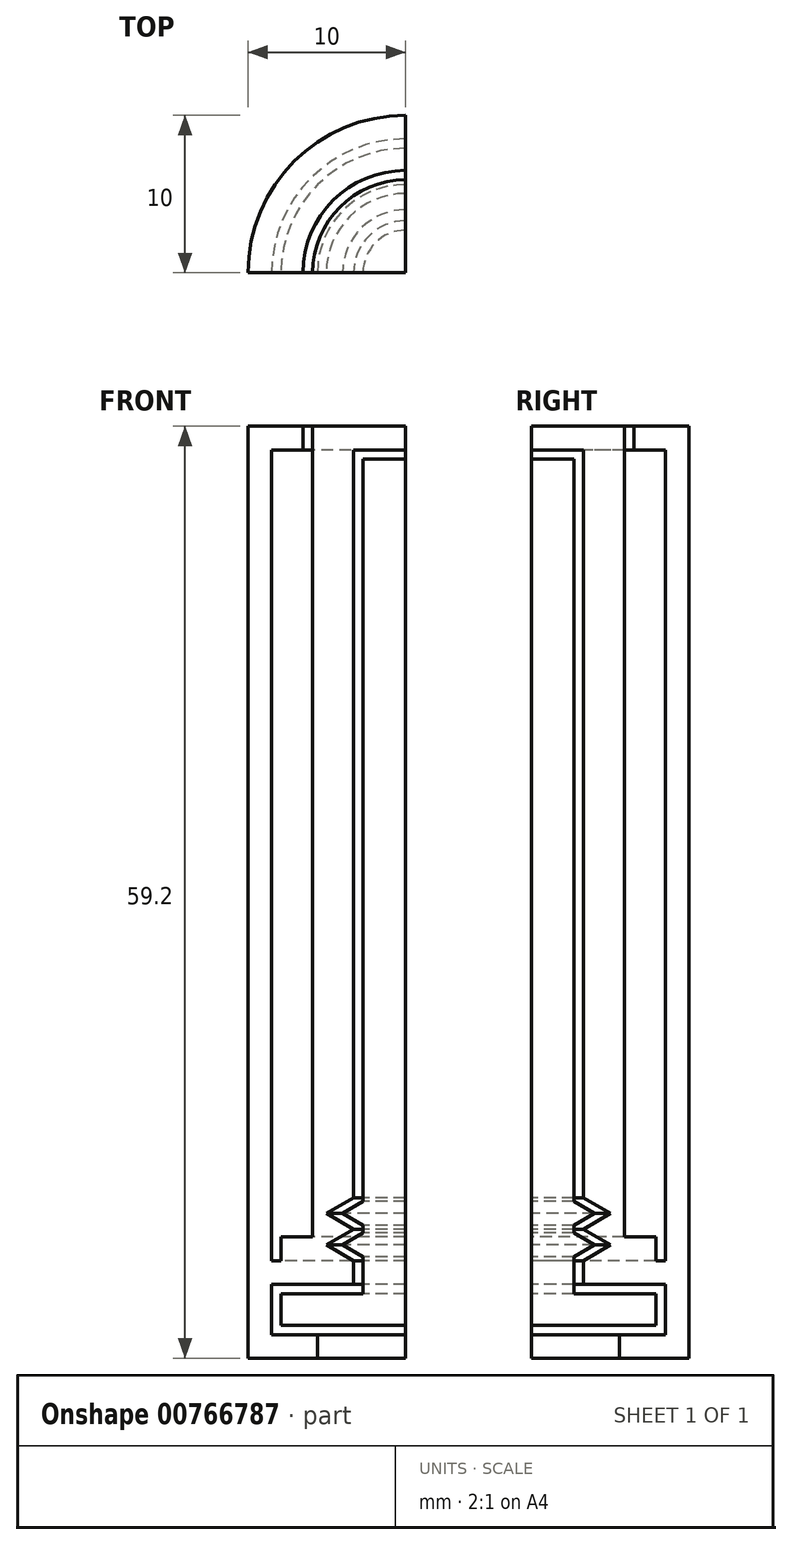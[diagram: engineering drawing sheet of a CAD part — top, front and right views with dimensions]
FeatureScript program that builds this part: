
annotation { "Feature Type Name" : "Feature", "Feature Type Description" : "" }
export const myFeature = defineFeature(function(context is Context, id is Id, definition is map)
    precondition{}
    {
        {
            var Q0;
            Q0=qCreatedBy(makeId("Front.planeOp"),FACE);
            var sketch = newSketch(context, id + "F0", { "sketchPlane" : qUnion([Q0])});
            skLineSegment(sketch, "E0", {"start": v(-3.3, -1.5) * mm, "end": v(-8.5, -1.5) * mm});
            skLineSegment(sketch, "E1", {"start": v(-8.5, -1.5) * mm, "end": v(-8.5, -4.7) * mm});
            skLineSegment(sketch, "E2", {"start": v(-8.5, -4.7) * mm, "end": v(-5.6, -4.7) * mm});
            skLineSegment(sketch, "E3", {"start": v(-5.6, -4.7) * mm, "end": v(-5.6, -6.2) * mm});
            skLineSegment(sketch, "E4", {"start": v(-5.6, -6.2) * mm, "end": v(-10, -6.2) * mm});
            skLineSegment(sketch, "E5", {"start": v(-10, -6.2) * mm, "end": v(-10, 53) * mm});
            skLineSegment(sketch, "E6", {"start": v(-10, 53) * mm, "end": v(-6.5, 53) * mm});
            skLineSegment(sketch, "E7", {"start": v(-6.5, 53) * mm, "end": v(-6.5, 51.5) * mm});
            skLineSegment(sketch, "E8", {"start": v(-6.5, 51.5) * mm, "end": v(-8.5, 51.5) * mm});
            skLineSegment(sketch, "E9", {"start": v(-8.5, 51.5) * mm, "end": v(-8.5, 0) * mm});
            skLineSegment(sketch, "E10", {"start": v(-8.5, 0) * mm, "end": v(-3.3, 0) * mm});
            skLineSegment(sketch, "E11", {"start": v(-3.3, 0) * mm, "end": v(-3.3, -1.5) * mm});
            skLineSegment(sketch, "E12", {"start": v(0, 50) * mm, "end": v(0, -50) * mm});
            skPoint(sketch, "E13", {"position": v(0, 0) * mm});
            skLineSegment(sketch, "E14", {"start": v(-7.9, 0) * mm, "end": v(-3.3, 0) * mm});
            skLineSegment(sketch, "E15", {"start": v(-3.3, 0) * mm, "end": v(-3.3, 51.5) * mm});
            skLineSegment(sketch, "E16", {"start": v(-3.3, 51.5) * mm, "end": v(0, 51.5) * mm});
            skLineSegment(sketch, "E17", {"start": v(0, 51.5) * mm, "end": v(0, 53) * mm});
            skLineSegment(sketch, "E18", {"start": v(0, 53) * mm, "end": v(-5.9, 53) * mm});
            skLineSegment(sketch, "E19", {"start": v(-5.9, 53) * mm, "end": v(-5.9, 1.5) * mm});
            skLineSegment(sketch, "E20", {"start": v(-5.9, 1.5) * mm, "end": v(-7.9, 1.5) * mm});
            skLineSegment(sketch, "E21", {"start": v(-7.9, 1.5) * mm, "end": v(-7.9, 0) * mm});
            skLineSegment(sketch, "E22", {"start": v(-3.3, 0) * mm, "end": v(-5.03, 1) * mm});
            skLineSegment(sketch, "E23", {"start": v(-5.03, 1) * mm, "end": v(-3.3, 2) * mm});
            skLineSegment(sketch, "E24", {"start": v(-3.3, 2) * mm, "end": v(-5.03, 3) * mm});
            skLineSegment(sketch, "E25", {"start": v(-5.03, 3) * mm, "end": v(-3.3, 4) * mm});
            skLineSegment(sketch, "E26", {"start": v(-7.9, -2.1) * mm, "end": v(-7.9, -4.1) * mm});
            skLineSegment(sketch, "E27", {"start": v(-7.9, -4.1) * mm, "end": v(0, -4.1) * mm});
            skLineSegment(sketch, "E28", {"start": v(0, -4.1) * mm, "end": v(0, 50.9) * mm});
            skLineSegment(sketch, "E29", {"start": v(0, 50.9) * mm, "end": v(-2.7, 50.9) * mm});
            skLineSegment(sketch, "E30", {"start": v(-2.7, 50.9) * mm, "end": v(-2.7, -2.1) * mm});
            skLineSegment(sketch, "E31", {"start": v(-2.7, -2.1) * mm, "end": v(-7.9, -2.1) * mm});
            skLineSegment(sketch, "E32", {"start": v(-2.7, 0.25) * mm, "end": v(-4, 1) * mm});
            skLineSegment(sketch, "E33", {"start": v(-4, 1) * mm, "end": v(-2.7, 1.75) * mm});
            skLineSegment(sketch, "E34", {"start": v(-2.7, 2.25) * mm, "end": v(-4, 3) * mm});
            skLineSegment(sketch, "E35", {"start": v(-4, 3) * mm, "end": v(-2.7, 3.75) * mm});
            skLineSegment(sketch, "E36", {"start": v(-2.7, 1.75) * mm, "end": v(-2.7, 2.25) * mm});
            skLineSegment(sketch, "E37", {"start": v(-2.7, 0.25) * mm, "end": v(-2.7, 0) * mm});
            skSolve(sketch);
        }
        {
            var Q0;
            Q0=makeQuery(id+"F0.imprint","IMPRINT",FACE,{"disambiguationData":[TD([[makeQuery(id+"F0.imprint","IMPRINT",EDGE,{"derivedFrom":sQuery(id+"F0.wireOp",EDGE,"E0")}),-1.0]])]});
            var Q1;
            {var subQ5=sQuery(id+"F0.wireOp",EDGE,"E16");Q1=makeQuery(id+"F0.imprint","IMPRINT",FACE,{"disambiguationData":[TD([[makeQuery(id+"F0.imprint","IMPRINT",EDGE,{"derivedFrom":subQ5}),1.0]])]});}
            var Q2;
            Q2=makeQuery(id+"F0.imprint","IMPRINT",FACE,{"disambiguationData":[TD([[makeQuery(id+"F0.imprint","IMPRINT",EDGE,{"derivedFrom":sQuery(id+"F0.wireOp",EDGE,"E26")}),1.0]])]});
            var Q3;
            {var subQ0=sQuery(id+"F0.wireOp",EDGE,"E32");var subQ1=sQuery(id+"F0.wireOp",EDGE,"E15");var subQ2=makeQuery(id+"F0.imprint","INTERSECT",VERTEX,{"derivedFrom":[subQ1,subQ0]});Q3=makeQuery(id+"F0.imprint","IMPRINT",FACE,{"disambiguationData":[TD([[makeQuery(id+"F0.imprint","IMPRINT",EDGE,{"disambiguationData":[TD([[subQ2,-1.0]])],"derivedFrom":subQ1}),1.0]])]});}
            var Q4;
            {var subQ0=sQuery(id+"F0.wireOp",EDGE,"E32");var subQ1=sQuery(id+"F0.wireOp",EDGE,"E15");var subQ2=makeQuery(id+"F0.imprint","INTERSECT",VERTEX,{"derivedFrom":[subQ1,subQ0]});Q4=makeQuery(id+"F0.imprint","IMPRINT",FACE,{"disambiguationData":[TD([[makeQuery(id+"F0.imprint","IMPRINT",EDGE,{"disambiguationData":[TD([[subQ2,-1.0]])],"derivedFrom":subQ1}),-1.0]])]});}
            var Q5;
            {var subQ0=sQuery(id+"F0.wireOp",EDGE,"E35");var subQ1=sQuery(id+"F0.wireOp",EDGE,"E15");var subQ2=makeQuery(id+"F0.imprint","INTERSECT",VERTEX,{"derivedFrom":[subQ1,subQ0]});Q5=makeQuery(id+"F0.imprint","IMPRINT",FACE,{"disambiguationData":[TD([[makeQuery(id+"F0.imprint","IMPRINT",EDGE,{"disambiguationData":[TD([[subQ2,1.0]])],"derivedFrom":subQ1}),1.0]])]});}
            var Q6;
            {var subQ0=sQuery(id+"F0.wireOp",EDGE,"E35");var subQ1=sQuery(id+"F0.wireOp",EDGE,"E15");var subQ2=makeQuery(id+"F0.imprint","INTERSECT",VERTEX,{"derivedFrom":[subQ1,subQ0]});Q6=makeQuery(id+"F0.imprint","IMPRINT",FACE,{"disambiguationData":[TD([[makeQuery(id+"F0.imprint","IMPRINT",EDGE,{"disambiguationData":[TD([[subQ2,1.0]])],"derivedFrom":subQ1}),-1.0]])]});}
            var Q7;
            Q7=sQuery(id+"F0.wireOp",EDGE,"E12");
            revolve(context, id + "F1", {"surfaceOperationType" : NewSurfaceOperationType.NEW, "entities" : qUnion([Q0, Q1, Q2, Q3, Q4, Q5, Q6]), "axis" : qUnion([Q7]), "revolveType" : RevolveType.ONE_DIRECTION, "angle" : 90 * degree});
        }
    });
